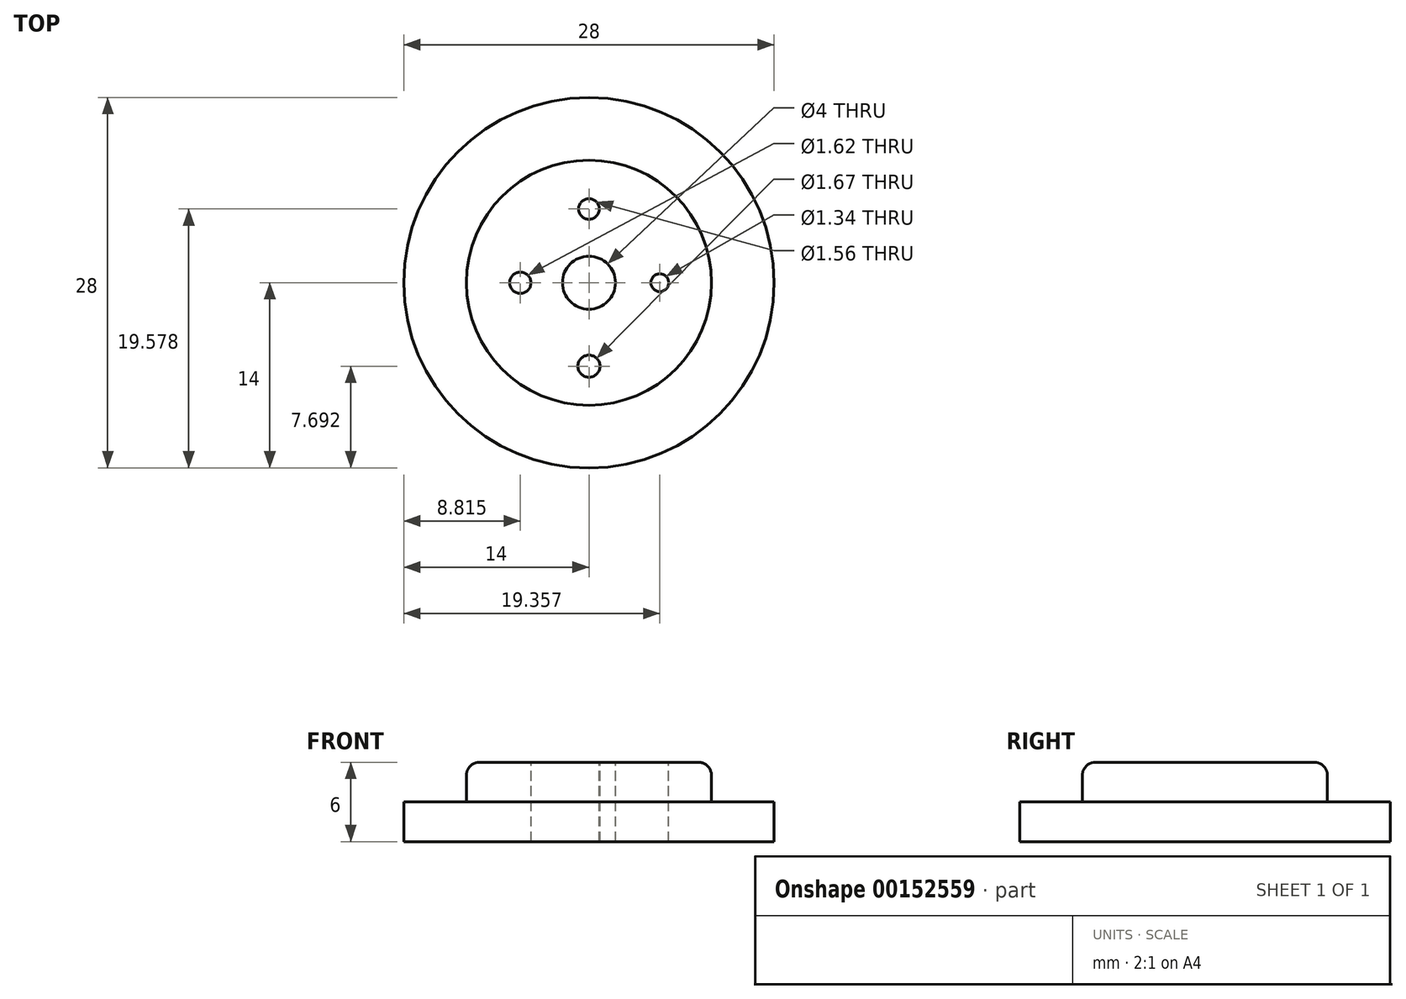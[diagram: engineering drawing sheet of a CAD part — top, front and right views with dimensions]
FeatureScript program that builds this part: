
annotation { "Feature Type Name" : "Feature", "Feature Type Description" : "" }
export const myFeature = defineFeature(function(context is Context, id is Id, definition is map)
    precondition{}
    {
        {
            var Q0;
            Q0=qCreatedBy(makeId("Top.planeOp"),FACE);
            var sketch = newSketch(context, id + "F0", { "sketchPlane" : qUnion([Q0])});
            skCircle(sketch, "E0", {"center": v(0, 0) * mm, "radius": 14 * mm});
            skSolve(sketch);
        }
        {
            var Q0;
            Q0=makeQuery(id+"F0.imprint","IMPRINT",FACE,{"disambiguationData":[TD([[makeQuery(id+"F0.imprint","IMPRINT",EDGE,{"derivedFrom":sQuery(id+"F0.wireOp",EDGE,"E0")}),1.0]])]});
            extrude(context, id + "F1", {"entities" : qUnion([Q0]), "depth" : 3 * mm});
        }
        {
            var Q0;
            Q0=makeQuery(id+"F1.opExtrude","CAP_FACE",FACE,{"disambiguationData":[OSD([sQuery(id+"F0.wireOp",EDGE,"E0")])],"isStart":false});
            var sketch = newSketch(context, id + "F2", { "sketchPlane" : qUnion([Q0])});
            skCircle(sketch, "E1", {"center": v(0, 0) * mm, "radius": 9.26 * mm});
            skSolve(sketch);
        }
        {
            var Q0;
            Q0=makeQuery(id+"F2.imprint","IMPRINT",FACE,{"disambiguationData":[TD([[makeQuery(id+"F2.imprint","IMPRINT",EDGE,{"derivedFrom":sQuery(id+"F2.wireOp",EDGE,"E1")}),1.0]])]});
            extrude(context, id + "F3", {"entities" : qUnion([Q0]), "operationType" : NewBodyOperationType.ADD, "depth" : 3 * mm});
        }
        {
            var Q0;
            Q0=makeQuery(id+"F3.opExtrude","CAP_FACE",FACE,{"disambiguationData":[OSD([sQuery(id+"F2.wireOp",EDGE,"E1")])],"isStart":false});
            var sketch = newSketch(context, id + "F4", { "sketchPlane" : qUnion([Q0])});
            skCircle(sketch, "E2", {"center": v(0, 0) * mm, "radius": 2 * mm});
            skSolve(sketch);
        }
        {
            var Q0;
            Q0=makeQuery(id+"F4.imprint","IMPRINT",FACE,{"disambiguationData":[TD([[makeQuery(id+"F4.imprint","IMPRINT",EDGE,{"derivedFrom":sQuery(id+"F4.wireOp",EDGE,"E2")}),1.0]])]});
            extrude(context, id + "F5", {"entities" : qUnion([Q0]), "operationType" : NewBodyOperationType.REMOVE, "oppositeDirection" : true, "depth" : 30 * mm});
        }
        {
            var Q0;
            Q0=makeQuery(id+"F3.opExtrude","CAP_FACE",FACE,{"disambiguationData":[OSD([sQuery(id+"F2.wireOp",EDGE,"E1")])],"isStart":false});
            var sketch = newSketch(context, id + "F6", { "sketchPlane" : qUnion([Q0])});
            skCircle(sketch, "E3", {"center": v(0, 5.58) * mm, "radius": 0.78 * mm});
            skCircle(sketch, "E4", {"center": v(5.36, 0) * mm, "radius": 0.67 * mm});
            skCircle(sketch, "E5", {"center": v(0, -6.3) * mm, "radius": 0.83 * mm});
            skCircle(sketch, "E6", {"center": v(-5.19, 0) * mm, "radius": 0.8 * mm});
            skSolve(sketch);
        }
        {
            var Q0;
            Q0 = qSketchRegion(id + "F6", true);
            extrude(context, id + "F7", {"entities" : qUnion([Q0]), "operationType" : NewBodyOperationType.REMOVE, "oppositeDirection" : true, "depth" : 25.4 * mm});
        }
        {
            var Q0;
            Q0=makeQuery(id+"F3.opExtrude","CAP_EDGE",EDGE,{"disambiguationData":[OSD([sQuery(id+"F2.wireOp",EDGE,"E1")])],"isStart":false});
            fillet(context, id + "F8", {"entities" : qUnion([Q0]), "radius" : 1 * mm, "tangentPropagation" : true, "allowEdgeOverflow" : false});
        }
    });
